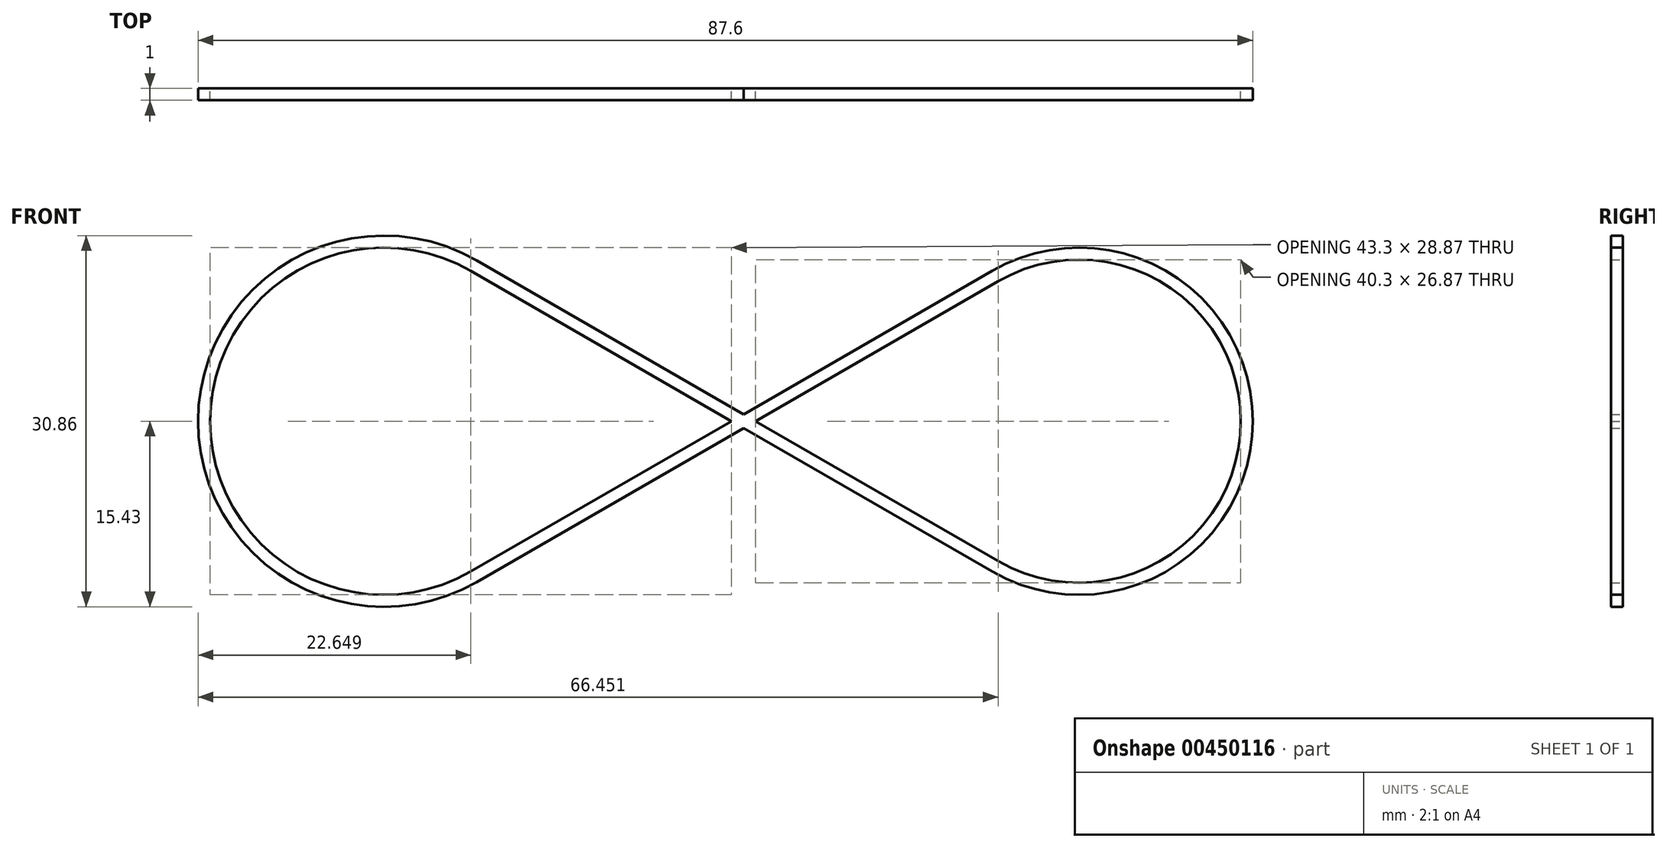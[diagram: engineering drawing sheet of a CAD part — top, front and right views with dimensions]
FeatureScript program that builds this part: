
annotation { "Feature Type Name" : "Feature", "Feature Type Description" : "" }
export const myFeature = defineFeature(function(context is Context, id is Id, definition is map)
    precondition{}
    {
        {
            var Q0;
            Q0=qCreatedBy(makeId("Front.planeOp"),FACE);
            var sketch = newSketch(context, id + "F0", { "sketchPlane" : qUnion([Q0])});
            skLineSegment(sketch, "E0", {"start": v(-25, 0) * mm, "end": v(25, 0) * mm, "construction": true});
            skLineSegment(sketch, "E1", {"start": v(0, -25) * mm, "end": v(0, 25) * mm, "construction": true});
            skCircle(sketch, "E2", {"center": v(0, 0) * mm, "radius": 25 * mm, "construction": true});
            skPoint(sketch, "E3.orphan", {"position": v(-43.48, 0) * mm});
            skPoint(sketch, "E4.orphan", {"position": v(0, -25.94) * mm});
            skLineSegment(sketch, "E5", {"start": v(-21.65, -12.5) * mm, "end": v(21.65, 12.5) * mm});
            skLineSegment(sketch, "E6.MirrorCS", {"start": v(-21.65, 12.5) * mm, "end": v(21.65, -12.5) * mm});
            skArc(sketch, "E7", {"start": v(21.65, -12.5) * mm, "mid": v(43.3, 0) * mm, "end": v(21.65, 12.5) * mm});
            skArc(sketch, "E8", {"start": v(-21.65, 12.5) * mm, "mid": v(-43.3, 0) * mm, "end": v(-21.65, -12.5) * mm});
            skArc(sketch, "E9.0", {"start": v(22.15, -11.63) * mm, "mid": v(42.3, 0) * mm, "end": v(22.15, 11.63) * mm});
            skLineSegment(sketch, "E9.1", {"start": v(-21.15, 13.37) * mm, "end": v(22.15, -11.63) * mm});
            skLineSegment(sketch, "E10.0", {"start": v(-21.15, -13.37) * mm, "end": v(22.15, 11.63) * mm});
            skArc(sketch, "E10.1", {"start": v(-21.15, 13.37) * mm, "mid": v(-44.3, 0) * mm, "end": v(-21.15, -13.37) * mm});
            skSolve(sketch);
        }
        {
            var Q0;
            Q0 = qSketchRegion(id + "F0", true);
            extrude(context, id + "F1", {"entities" : qUnion([Q0]), "depth" : 1 * mm});
        }
    });
